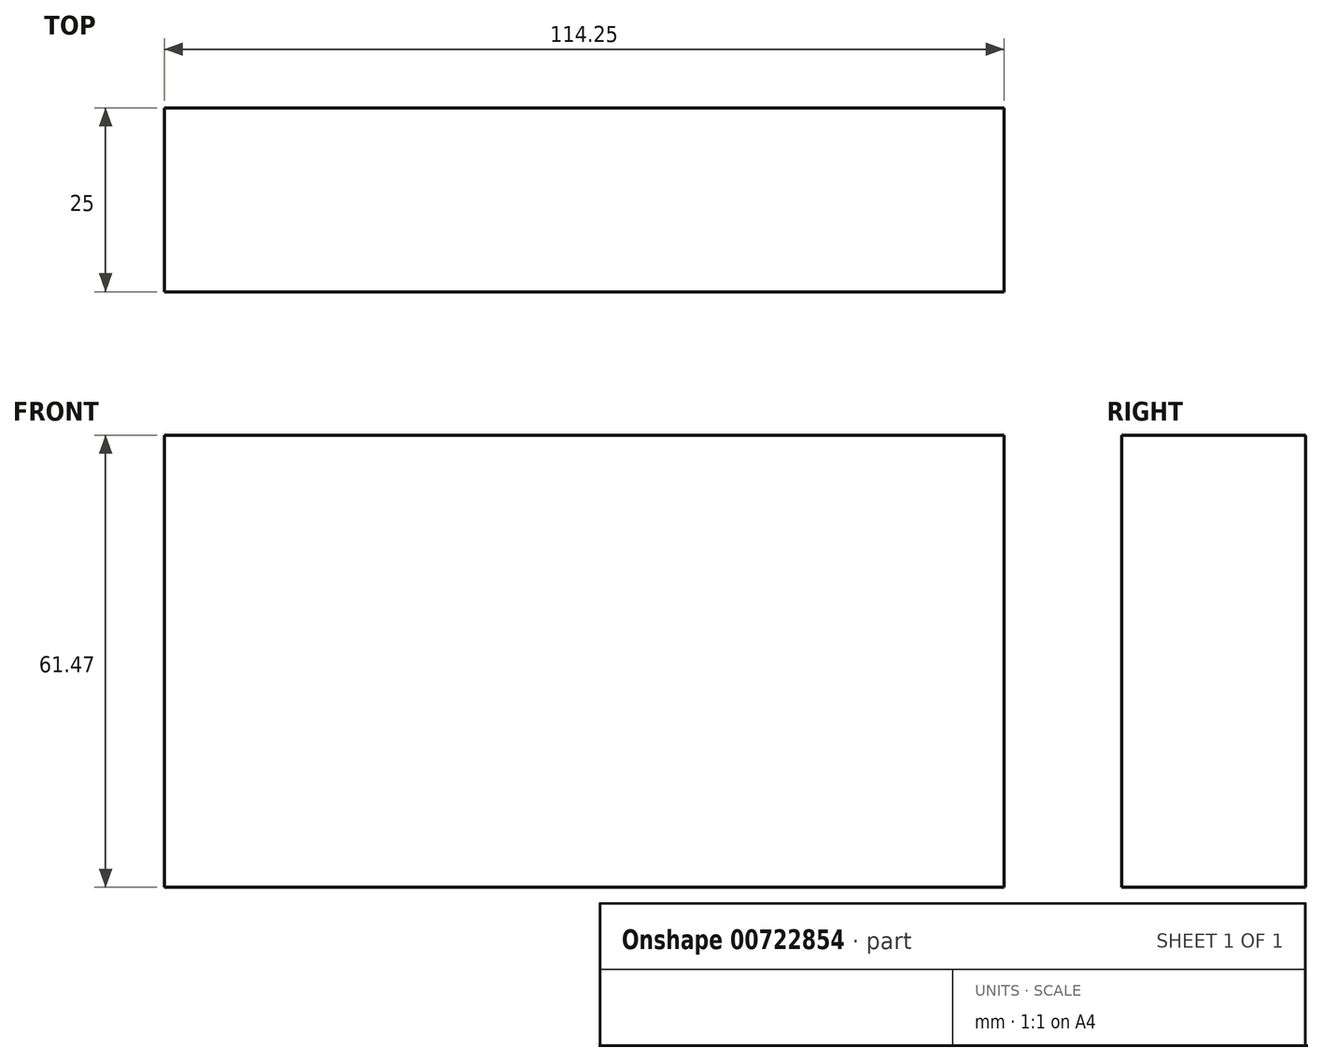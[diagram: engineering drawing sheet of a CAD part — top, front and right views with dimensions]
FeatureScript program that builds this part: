
annotation { "Feature Type Name" : "Feature", "Feature Type Description" : "" }
export const myFeature = defineFeature(function(context is Context, id is Id, definition is map)
    precondition{}
    {
        {
            var Q0;
            Q0=qCreatedBy(makeId("Front.planeOp"),FACE);
            var sketch = newSketch(context, id + "F0", { "sketchPlane" : qUnion([Q0])});
            skLineSegment(sketch, "E0.bottom", {"start": v(-90.39, 42.88) * mm, "end": v(23.86, 42.88) * mm});
            skLineSegment(sketch, "E0.top", {"start": v(-90.39, -18.6) * mm, "end": v(23.86, -18.6) * mm});
            skLineSegment(sketch, "E0.left", {"start": v(-90.39, 42.88) * mm, "end": v(-90.39, -18.6) * mm});
            skLineSegment(sketch, "E0.right", {"start": v(23.86, 42.88) * mm, "end": v(23.86, -18.6) * mm});
            skSolve(sketch);
        }
        {
            var Q0;
            Q0 = qSketchRegion(id + "F0", true);
            extrude(context, id + "F1", {"entities" : qUnion([Q0]), "depth" : 25 * mm, "offsetDistance" : 25 * mm});
        }
    });
